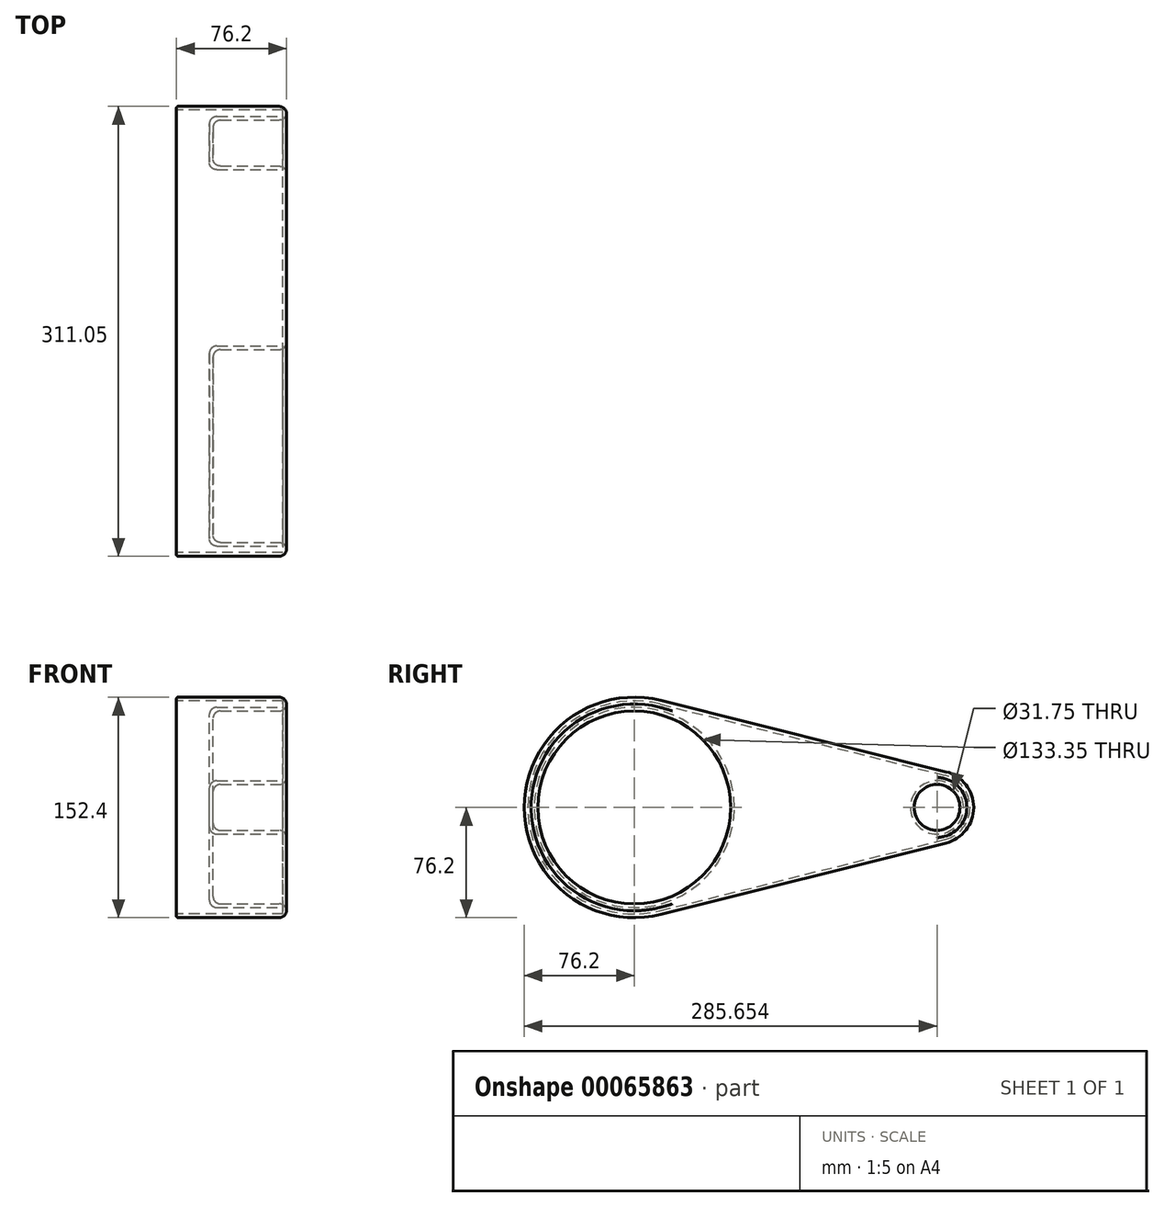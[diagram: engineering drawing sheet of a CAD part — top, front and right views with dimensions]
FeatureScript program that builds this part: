
annotation { "Feature Type Name" : "Feature", "Feature Type Description" : "" }
export const myFeature = defineFeature(function(context is Context, id is Id, definition is map)
    precondition{}
    {
        {
            var Q0;
            Q0=qCreatedBy(makeId("Right.planeOp"),FACE);
            var sketch = newSketch(context, id + "F0", { "sketchPlane" : qUnion([Q0])});
            skCircle(sketch, "E0", {"center": v(0, 0) * mm, "radius": 76.2 * mm});
            skCircle(sketch, "E1", {"center": v(209.45, 0) * mm, "radius": 25.4 * mm});
            skLineSegment(sketch, "E2", {"start": v(18.48, 73.92) * mm, "end": v(215.61, 24.64) * mm});
            skLineSegment(sketch, "E3", {"start": v(18.48, -73.92) * mm, "end": v(215.61, -24.64) * mm});
            skSolve(sketch);
        }
        {
            var Q0;
            {var subQ0=sQuery(id+"F0.wireOp",EDGE,"E2");Q0=makeQuery(id+"F0.imprint","IMPRINT",FACE,{"disambiguationData":[TD([[makeQuery(id+"F0.imprint","IMPRINT",EDGE,{"derivedFrom":subQ0}),-1.0]])]});}
            var Q1;
            {var subQ0=sQuery(id+"F0.wireOp",EDGE,"E0");var subQ1=makeQuery(id+"F0.imprint","INTERSECT",VERTEX,{"derivedFrom":[subQ0,sQuery(id+"F0.wireOp",EDGE,"E2")]});Q1=makeQuery(id+"F0.imprint","IMPRINT",FACE,{"disambiguationData":[TD([[makeQuery(id+"F0.imprint","IMPRINT",EDGE,{"disambiguationData":[TD([[subQ1,-1.0]])],"derivedFrom":subQ0}),1.0]])]});}
            var Q2;
            {var subQ0=sQuery(id+"F0.wireOp",EDGE,"E1");var subQ1=makeQuery(id+"F0.imprint","INTERSECT",VERTEX,{"derivedFrom":[subQ0,sQuery(id+"F0.wireOp",EDGE,"E2")]});Q2=makeQuery(id+"F0.imprint","IMPRINT",FACE,{"disambiguationData":[TD([[makeQuery(id+"F0.imprint","IMPRINT",EDGE,{"disambiguationData":[TD([[subQ1,-1.0]])],"derivedFrom":subQ0}),1.0]])]});}
            extrude(context, id + "F1", {"entities" : qUnion([Q0, Q1, Q2]), "depth" : 76.2 * mm});
        }
        {
            var Q0;
            Q0=makeQuery(id+"F1.opExtrude","CAP_FACE",FACE,{"disambiguationData":[OSD([sQuery(id+"F0.wireOp",EDGE,"E0"),sQuery(id+"F0.wireOp",EDGE,"E1"),sQuery(id+"F0.wireOp",EDGE,"E2"),sQuery(id+"F0.wireOp",EDGE,"E3")])],"isStart":false});
            var sketch = newSketch(context, id + "F2", { "sketchPlane" : qUnion([Q0])});
            skCircle(sketch, "E4", {"center": v(0, 0) * mm, "radius": 66.68 * mm});
            skCircle(sketch, "E5", {"center": v(209.45, 0) * mm, "radius": 15.88 * mm});
            skSolve(sketch);
        }
        {
            var Q0;
            Q0=makeQuery(id+"F2.imprint","IMPRINT",FACE,{"disambiguationData":[TD([[makeQuery(id+"F2.imprint","IMPRINT",EDGE,{"derivedFrom":sQuery(id+"F2.wireOp",EDGE,"E4")}),1.0]])]});
            var Q1;
            Q1=makeQuery(id+"F2.imprint","IMPRINT",FACE,{"disambiguationData":[TD([[makeQuery(id+"F2.imprint","IMPRINT",EDGE,{"derivedFrom":sQuery(id+"F2.wireOp",EDGE,"E5")}),1.0]])]});
            extrude(context, id + "F3", {"entities" : qUnion([Q0, Q1]), "operationType" : NewBodyOperationType.REMOVE, "oppositeDirection" : true, "depth" : 50.8 * mm});
        }
        {
            var Q0;
            Q0=makeQuery(id+"F1.opExtrude","CAP_FACE",FACE,{"disambiguationData":[OSD([sQuery(id+"F0.wireOp",EDGE,"E0"),sQuery(id+"F0.wireOp",EDGE,"E1"),sQuery(id+"F0.wireOp",EDGE,"E2"),sQuery(id+"F0.wireOp",EDGE,"E3")])],"isStart":true});
            shell(context, id + "F4", {"entities" : qUnion([Q0]), "thickness" : 2.54 * mm});
        }
        {
            var Q0;
            Q0=makeQuery(id+"F1.opExtrude","CAP_FACE",FACE,{"disambiguationData":[OSD([sQuery(id+"F0.wireOp",EDGE,"E0"),sQuery(id+"F0.wireOp",EDGE,"E1"),sQuery(id+"F0.wireOp",EDGE,"E2"),sQuery(id+"F0.wireOp",EDGE,"E3")])],"isStart":false});
            var Q1;
            Q1=makeQuery(id+"F3.boolean.opBoolean","COPY",EDGE,{"derivedFrom":makeQuery(id+"F3.opExtrude","CAP_EDGE",EDGE,{"disambiguationData":[OSD([sQuery(id+"F2.wireOp",EDGE,"E4")])],"isStart":false})});
            var Q2;
            Q2=makeQuery(id+"F3.boolean.opBoolean","COPY",EDGE,{"derivedFrom":makeQuery(id+"F3.opExtrude","CAP_EDGE",EDGE,{"disambiguationData":[OSD([sQuery(id+"F2.wireOp",EDGE,"E5")])],"isStart":false})});
            fillet(context, id + "F5", {"entities" : qUnion([Q0, Q1, Q2]), "radius" : 5.08 * mm, "tangentPropagation" : true, "allowEdgeOverflow" : false});
        }
        {
            var Q0;
            {var subQ0=sQuery(id+"F0.wireOp",EDGE,"E0");Q0=makeQuery(id+"F4.opShell","OFFSET_EDGE",EDGE,{"disambiguationData":[OSD([subQ0]),TDD([makeQuery(id+"F1.opExtrude","CAP_EDGE",EDGE,{"disambiguationData":[OSD([subQ0])],"isStart":true})])]});}
            var Q1;
            {var subQ0=sQuery(id+"F0.wireOp",EDGE,"E3");Q1=makeQuery(id+"F4.opShell","OFFSET_EDGE",EDGE,{"disambiguationData":[OSD([subQ0]),TDD([makeQuery(id+"F1.opExtrude","CAP_EDGE",EDGE,{"disambiguationData":[OSD([subQ0])],"isStart":true})])]});}
            var Q2;
            {var subQ0=sQuery(id+"F0.wireOp",EDGE,"E1");Q2=makeQuery(id+"F4.opShell","OFFSET_EDGE",EDGE,{"disambiguationData":[OSD([subQ0]),TDD([makeQuery(id+"F1.opExtrude","CAP_EDGE",EDGE,{"disambiguationData":[OSD([subQ0])],"isStart":true})])]});}
            var Q3;
            {var subQ0=sQuery(id+"F0.wireOp",EDGE,"E2");Q3=makeQuery(id+"F4.opShell","OFFSET_EDGE",EDGE,{"disambiguationData":[OSD([subQ0]),TDD([makeQuery(id+"F1.opExtrude","CAP_EDGE",EDGE,{"disambiguationData":[OSD([subQ0])],"isStart":true})])]});}
            var Q4;
            Q4=makeQuery(id+"F1.opExtrude","CAP_EDGE",EDGE,{"disambiguationData":[OSD([sQuery(id+"F0.wireOp",EDGE,"E2")])],"isStart":true});
            var Q5;
            Q5=makeQuery(id+"F1.opExtrude","CAP_EDGE",EDGE,{"disambiguationData":[OSD([sQuery(id+"F0.wireOp",EDGE,"E1")])],"isStart":true});
            var Q6;
            Q6=makeQuery(id+"F1.opExtrude","CAP_EDGE",EDGE,{"disambiguationData":[OSD([sQuery(id+"F0.wireOp",EDGE,"E3")])],"isStart":true});
            var Q7;
            Q7=makeQuery(id+"F1.opExtrude","CAP_EDGE",EDGE,{"disambiguationData":[OSD([sQuery(id+"F0.wireOp",EDGE,"E0")])],"isStart":true});
            fillet(context, id + "F6", {"entities" : qUnion([Q0, Q1, Q2, Q3, Q4, Q5, Q6, Q7]), "radius" : 1.27 * mm, "tangentPropagation" : true, "allowEdgeOverflow" : false});
        }
        {
            var Q0;
            {var subQ0=sQuery(id+"F2.wireOp",EDGE,"E4");Q0=makeQuery(id+"F4.opShell","OFFSET_FACE",FACE,{"disambiguationData":[OSD([subQ0]),TDD([makeQuery(id+"F3.boolean.opBoolean","COPY",FACE,{"derivedFrom":makeQuery(id+"F3.opExtrude","CAP_FACE",FACE,{"disambiguationData":[OSD([subQ0])],"isStart":false})})])]});}
            var Q1;
            {var subQ0=sQuery(id+"F2.wireOp",EDGE,"E5");Q1=makeQuery(id+"F4.opShell","OFFSET_FACE",FACE,{"disambiguationData":[OSD([subQ0]),TDD([makeQuery(id+"F3.boolean.opBoolean","COPY",FACE,{"derivedFrom":makeQuery(id+"F3.opExtrude","CAP_FACE",FACE,{"disambiguationData":[OSD([subQ0])],"isStart":false})})])]});}
            fillet(context, id + "F7", {"entities" : qUnion([Q0, Q1]), "radius" : 5.08 * mm, "tangentPropagation" : true, "allowEdgeOverflow" : false});
        }
    });
